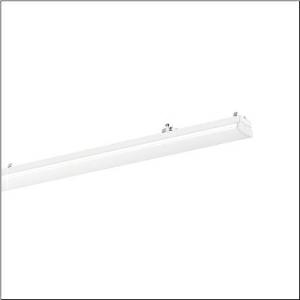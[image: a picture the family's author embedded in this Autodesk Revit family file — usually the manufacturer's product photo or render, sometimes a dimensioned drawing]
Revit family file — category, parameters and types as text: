
# Revit family: licross_r__11_recessed_opal_ho_51te1ddv4m1m_bc4c
name_source: partatom
category: Lighting Fixtures
units: mm (PartAtom-declared; Revit-internal decimal feet)

## family parameters
Cut with Voids When Loaded = No
Host = Face
Light Source = No
Part Type = Normal
Room Calculation Point = No
Round Connector Dimension = Use Diameter
Shared = No

## types (1)
- --- (1 x LED, 26350 lm, 150.5 W, 4000K)
    Apparent Load = 150 VA
    CIE Flux Codes = 44 73 91 87 100
    Color Rendering = 80
    Color Temperature = 4000K
    Default Elevation = 1800 mm
    Description = Licross® 11 recessed opal HO, luminaire insert, of sheet steel, coil coated, white, length: 2.250mm, width: 76mm, height: 87mm, LED rated luminous flux: 26.350lm, light colour: 840, control gear: DALI 2, with plug, 5-pole, with phase selection, mains connection: 220..240V, AC, 50/60Hz, rated input power: 151W, internal wiring halogen-free, primary optical cover: cover, of PMMA, light emission: direct with ceiling illumination distribution, primary light characteristic: symmetric, protection rating (complete): IP54, insulation class (complete): insulation class I (protective earthing), certification: CE, ENEC, VDE, UKCA, protection symbol: D if used in an environment with non-conductive dust loads with corresponding accessories, impact resistance: IK06, permissible ambient temperature for indoor applications: -40..+35°C, corresponds to IFS (International Featured Standards) requirements for safety and quality in the food industry, reducing of maximum allowable ambient temperature of 5°C with ceiling mounting, LABS conformity tested according to VDMA 24364:2018-05, packaging unit: 1 piece
    Height = 83 mm
    Lamp = 1 x LED
    Lamp Light Flux = 26350 lm
    Lamp Power = 150.5 W
    Lamp count = 1
    Length = 2250 mm
    Luminous efficacy = 175 lm/W
    Manufacturer = Siteco
    ModVariant = No
    Model = 51TE1DDV4M1M
    Mounting Place = Ceiling
    Mounting Type = Pendant
    Number of Poles = 1
    OnlyDefault = Yes
    Power Factor = 1
    Product Name = Licross® 11 recessed opal HO
    Product group = luminaire insert | ceiling pendant
    ProductGroupID = 902
    Protection Class = Protection class I
    Protection Degree = IP 54
    RLX_Detail_Level = 1
    RLX_Emergency_Light_Flux = 0 lm
    RLX_Emergency_Type = 0
    RLX_Emergency_Type_DB = No
    RlxData = <blob elided: 27013 chars, md5=6d2a1e15>
    Socket = socket
    Standby Power = 0 W
    System Light Flux = 26350 lm
    System Power = 150 W
    Type Comments = factory setting: luminous flux: 100 % | dim-lin: 254 | 690 mA
    Type Image = l_1313666.jpg
    URL = http://relux.com
    VarID = @adj_097827
    Voltage = 0 V
    Weight = 0.00 kg
    Width = 76 mm

## geometry (parser evidence)
native form markers: Blend x4, Sweep x13
no freeform markers — native parametric forms only
